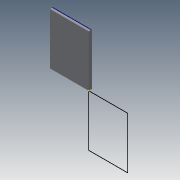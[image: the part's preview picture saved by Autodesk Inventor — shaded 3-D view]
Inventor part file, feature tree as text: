
AUTODESK INVENTOR PART (.ipt)
format: ipt  version: 2015 (Build 190159000, 159)  size: 80,384 bytes
history: native  units: mm
features: other x5, sketch x2, extrude x1, projected_geometry x1
ambient origin geometry x8: Origin, YZ Plane, XZ Plane, XY Plane, X Axis, Y Axis, Z Axis, Center Point
bodies: Solid1 (feature_tree)
feature tree (9):
  other  "Blocks"
  extrude  "Extrusion1"  Depth=150.0mm
  sketch  "Sketch2"  dims[d2=10.0mm d3=0.0mm]
  other  "DXF"
  sketch  "Sketch1"  dims[d0=200.0mm d1=150.0mm]
  projected_geometry  "Projected Loop1"
  other  "Block1"
  other  "Block1:1"
  other  "Block1:2"
